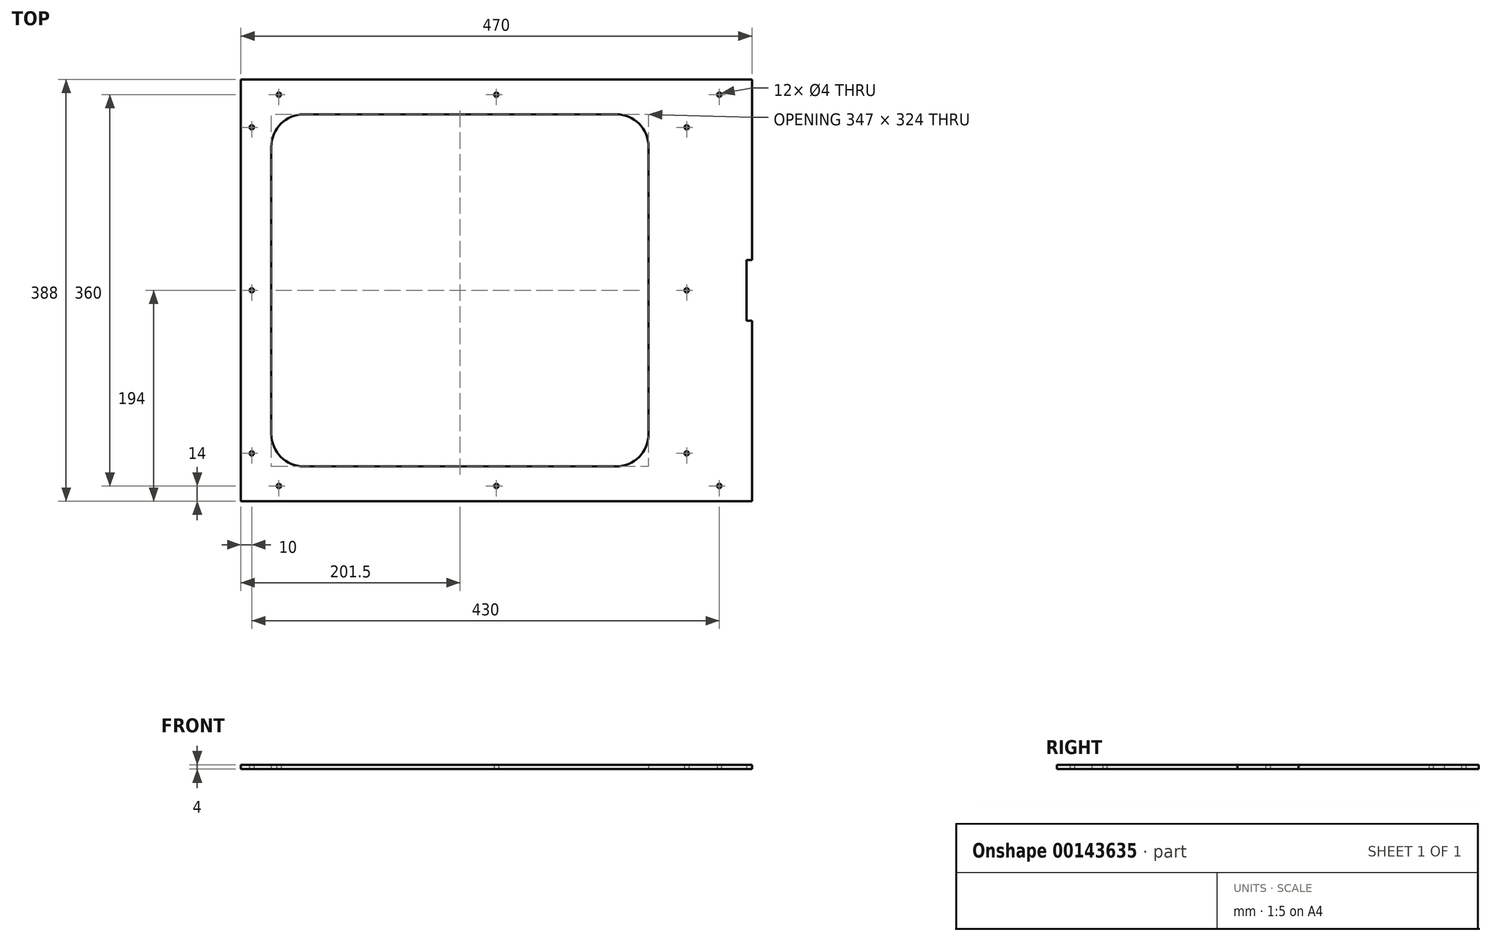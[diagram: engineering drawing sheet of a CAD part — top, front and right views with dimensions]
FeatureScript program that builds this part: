
annotation { "Feature Type Name" : "Feature", "Feature Type Description" : "" }
export const myFeature = defineFeature(function(context is Context, id is Id, definition is map)
    precondition{}
    {
        {
            var Q0;
            Q0=qCreatedBy(makeId("Top.planeOp"),FACE);
            var sketch = newSketch(context, id + "F0", { "sketchPlane" : qUnion([Q0])});
            skLineSegment(sketch, "E0.bottom", {"start": v(-235, 190) * mm, "end": v(235, 190) * mm, "construction": true});
            skLineSegment(sketch, "E0.top", {"start": v(-235, -190) * mm, "end": v(235, -190) * mm, "construction": true});
            skLineSegment(sketch, "E0.left", {"start": v(-235, 190) * mm, "end": v(-235, -190) * mm});
            skLineSegment(sketch, "E0.right", {"start": v(235, 190) * mm, "end": v(235, 28) * mm});
            skPoint(sketch, "E0.middle", {"position": v(0, 0) * mm});
            skLineSegment(sketch, "E1.bottom", {"start": v(-235, -190) * mm, "end": v(-215, -190) * mm});
            skLineSegment(sketch, "E1.top", {"start": v(-235, -170) * mm, "end": v(-215, -170) * mm, "construction": true});
            skLineSegment(sketch, "E1.left", {"start": v(-235, -190) * mm, "end": v(-235, -170) * mm});
            skLineSegment(sketch, "E1.right", {"start": v(-215, -190) * mm, "end": v(-215, -170) * mm, "construction": true});
            skLineSegment(sketch, "E2", {"start": v(-235, 0) * mm, "end": v(-215, 0) * mm, "construction": true});
            skLineSegment(sketch, "E3", {"start": v(0, -190) * mm, "end": v(0, 0) * mm, "construction": true});
            skLineSegment(sketch, "E4.MirrorCS", {"start": v(-215, 190) * mm, "end": v(-215, 170) * mm, "construction": true});
            skLineSegment(sketch, "E5.MirrorCS", {"start": v(235, -170) * mm, "end": v(215, -170) * mm, "construction": true});
            skLineSegment(sketch, "E6", {"start": v(-215, -170) * mm, "end": v(175, -170) * mm, "construction": true});
            skLineSegment(sketch, "E7", {"start": v(-215, -170) * mm, "end": v(-215, 0) * mm, "construction": true});
            skLineSegment(sketch, "E8.top", {"start": v(235, 194) * mm, "end": v(-235, 194) * mm});
            skLineSegment(sketch, "E8.left", {"start": v(235, 190) * mm, "end": v(235, 194) * mm});
            skLineSegment(sketch, "E8.right", {"start": v(-235, 190) * mm, "end": v(-235, 194) * mm});
            skLineSegment(sketch, "E9.MirrorCS", {"start": v(235, -194) * mm, "end": v(-235, -194) * mm});
            skLineSegment(sketch, "E10.MirrorCS", {"start": v(-235, -190) * mm, "end": v(-235, -194) * mm});
            skPoint(sketch, "E11", {"position": v(175, -194) * mm});
            skLineSegment(sketch, "E12", {"start": v(175, -194) * mm, "end": v(175, -190) * mm, "construction": true});
            skLineSegment(sketch, "E13.bottom", {"start": v(-177, -162) * mm, "end": v(110, -162) * mm});
            skLineSegment(sketch, "E13.left", {"start": v(-207, -132) * mm, "end": v(-207, 0) * mm});
            skLineSegment(sketch, "E13.right", {"start": v(140, -132) * mm, "end": v(140, 0) * mm});
            skPoint(sketch, "E14.visualSharp", {"position": v(-207, -162) * mm});
            skArc(sketch, "E14.filletArc", {"start": v(-207, -132) * mm, "mid": v(-198.21, -153.21) * mm, "end": v(-177, -162) * mm});
            skPoint(sketch, "E15.visualSharp", {"position": v(140, -162) * mm});
            skArc(sketch, "E15.filletArc", {"start": v(110, -162) * mm, "mid": v(131.21, -153.21) * mm, "end": v(140, -132) * mm});
            skLineSegment(sketch, "E16.MirrorCS", {"start": v(-207, 132) * mm, "end": v(-207, 0) * mm});
            skArc(sketch, "E17.MirrorCS", {"start": v(-207, 132) * mm, "mid": v(-198.21, 153.21) * mm, "end": v(-177, 162) * mm});
            skLineSegment(sketch, "E18.MirrorCS", {"start": v(-177, 162) * mm, "end": v(110, 162) * mm});
            skLineSegment(sketch, "E19.MirrorCS", {"start": v(140, 132) * mm, "end": v(140, 0) * mm});
            skArc(sketch, "E20.MirrorCS", {"start": v(110, 162) * mm, "mid": v(131.21, 153.21) * mm, "end": v(140, 132) * mm});
            skLineSegment(sketch, "E21", {"start": v(235, -190) * mm, "end": v(235, -194) * mm});
            skCircle(sketch, "E22", {"center": v(175, 0) * mm, "radius": 2 * mm});
            skLineSegment(sketch, "E23", {"start": v(175, -170) * mm, "end": v(215, -170) * mm, "construction": true});
            skLineSegment(sketch, "E24", {"start": v(175, -190) * mm, "end": v(175, -170) * mm, "construction": true});
            skLineSegment(sketch, "E25", {"start": v(175, -170) * mm, "end": v(175, -130) * mm, "construction": true});
            skLineSegment(sketch, "E26", {"start": v(175, -130) * mm, "end": v(175, 194) * mm, "construction": true});
            skCircle(sketch, "E27", {"center": v(175, -150) * mm, "radius": 2 * mm});
            skLineSegment(sketch, "E28", {"start": v(175, -180) * mm, "end": v(-20, -180) * mm, "construction": true});
            skLineSegment(sketch, "E29", {"start": v(175, -180) * mm, "end": v(235, -180) * mm, "construction": true});
            skCircle(sketch, "E30", {"center": v(205, -180) * mm, "radius": 2 * mm});
            skLineSegment(sketch, "E31", {"start": v(-20, -180) * mm, "end": v(-215, -180) * mm, "construction": true});
            skCircle(sketch, "E32.MirrorC", {"center": v(205, 180) * mm, "radius": 2 * mm});
            skCircle(sketch, "E33.MirrorC", {"center": v(-200, 180) * mm, "radius": 2 * mm});
            skLineSegment(sketch, "E34.MirrorCS", {"start": v(0, 190) * mm, "end": v(0, 0) * mm, "construction": true});
            skLineSegment(sketch, "E35.MirrorCS", {"start": v(235, -190) * mm, "end": v(235, -28) * mm});
            skLineSegment(sketch, "E36.MirrorCS", {"start": v(175, 190) * mm, "end": v(175, 170) * mm, "construction": true});
            skLineSegment(sketch, "E37.MirrorCS", {"start": v(175, 180) * mm, "end": v(235, 180) * mm, "construction": true});
            skCircle(sketch, "E38.MirrorC", {"center": v(175, 150) * mm, "radius": 2 * mm});
            skLineSegment(sketch, "E39", {"start": v(-215, 0) * mm, "end": v(-215, 170) * mm, "construction": true});
            skLineSegment(sketch, "E40", {"start": v(-215, 0) * mm, "end": v(-137.24, 0) * mm, "construction": true});
            skCircle(sketch, "E41", {"center": v(-225, 0) * mm, "radius": 2 * mm});
            skCircle(sketch, "E42", {"center": v(-225, 150) * mm, "radius": 2 * mm});
            skLineSegment(sketch, "E43", {"start": v(175, 180) * mm, "end": v(0, 180) * mm, "construction": true});
            skLineSegment(sketch, "E44", {"start": v(0, 180) * mm, "end": v(-215, 180) * mm, "construction": true});
            skCircle(sketch, "E45", {"center": v(0, 180) * mm, "radius": 2 * mm});
            skCircle(sketch, "E46.MirrorC", {"center": v(-225, -150) * mm, "radius": 2 * mm});
            skCircle(sketch, "E47.MirrorC", {"center": v(0, -180) * mm, "radius": 2 * mm});
            skCircle(sketch, "E48.MirrorC", {"center": v(-200, -180) * mm, "radius": 2 * mm});
            skLineSegment(sketch, "E49.bottom", {"start": v(174.03, 303.47) * mm, "end": v(174.03, 401.6) * mm});
            skLineSegment(sketch, "E49.top", {"start": v(214.76, 303.47) * mm, "end": v(214.76, 401.6) * mm});
            skCircle(sketch, "E50.MirrorC", {"center": v(191.67, 426.9) * mm, "radius": 10 * mm});
            skCircle(sketch, "E51", {"center": v(213.18, 437.38) * mm, "radius": 1.5 * mm});
            skLineSegment(sketch, "E49.left", {"start": v(174.03, 303.47) * mm, "end": v(214.76, 303.47) * mm});
            skCircle(sketch, "E52", {"center": v(213.18, 292.2) * mm, "radius": 1.5 * mm});
            skLineSegment(sketch, "E49.right", {"start": v(174.03, 401.6) * mm, "end": v(214.76, 401.6) * mm});
            skCircle(sketch, "E53", {"center": v(163.23, 292.38) * mm, "radius": 1.5 * mm});
            skCircle(sketch, "E54", {"center": v(163.18, 437.38) * mm, "radius": 1.5 * mm});
            skLineSegment(sketch, "E55.top", {"start": v(235, 28) * mm, "end": v(230, 28) * mm});
            skLineSegment(sketch, "E55.right", {"start": v(230, 0) * mm, "end": v(230, 28) * mm});
            skLineSegment(sketch, "E56.MirrorCS", {"start": v(230, 0) * mm, "end": v(230, -28) * mm});
            skLineSegment(sketch, "E57.MirrorCS", {"start": v(235, -28) * mm, "end": v(230, -28) * mm});
            skLineSegment(sketch, "E58.trimOffspring", {"start": v(235, -28) * mm, "end": v(235, -190) * mm});
            skLineSegment(sketch, "E59.trimOffspring", {"start": v(235, 28) * mm, "end": v(235, 190) * mm});
            skSolve(sketch);
        }
        {
            var Q0;
            Q0=makeQuery(id+"F0.imprint","IMPRINT",FACE,{"disambiguationData":[TD([[makeQuery(id+"F0.imprint","IMPRINT",EDGE,{"derivedFrom":sQuery(id+"F0.wireOp",EDGE,"209ff420-4bb6-4f9b-a423-d3239ede89f50.MirrorC")}),-1.0]])]});
            var Q1;
            {var subQ2=sQuery(id+"F0.wireOp",EDGE,"E1.right");Q1=makeQuery(id+"F0.imprint","IMPRINT",FACE,{"disambiguationData":[TD([[makeQuery(id+"F0.imprint","IMPRINT",EDGE,{"derivedFrom":subQ2}),-1.0]])]});}
            var Q2;
            Q2=makeQuery(id+"F0.imprint","IMPRINT",FACE,{"disambiguationData":[TD([[makeQuery(id+"F0.imprint","IMPRINT",EDGE,{"derivedFrom":sQuery(id+"F0.wireOp",EDGE,"wbOcR5t3-yBRG-kf52-RCKl-xsM90Xmz3qXt")}),1.0]])]});
            var Q3;
            {var subQ0=sQuery(id+"F0.wireOp",EDGE,"E1.top");Q3=makeQuery(id+"F0.imprint","IMPRINT",FACE,{"disambiguationData":[TD([[makeQuery(id+"F0.imprint","IMPRINT",EDGE,{"derivedFrom":subQ0}),1.0]])]});}
            var Q4;
            Q4=makeQuery(id+"F0.imprint","IMPRINT",FACE,{"disambiguationData":[TD([[makeQuery(id+"F0.imprint","IMPRINT",EDGE,{"derivedFrom":sQuery(id+"F0.wireOp",EDGE,"E1.bottom")}),1.0]])]});
            var Q5;
            {var subQ3=sQuery(id+"F0.wireOp",EDGE,"E4.MirrorCS");Q5=makeQuery(id+"F0.imprint","IMPRINT",FACE,{"disambiguationData":[TD([[makeQuery(id+"F0.imprint","IMPRINT",EDGE,{"derivedFrom":subQ3}),-1.0]])]});}
            var Q6;
            {var subQ0=sQuery(id+"F0.wireOp",EDGE,"E1.bottom");Q6=makeQuery(id+"F0.imprint","IMPRINT",FACE,{"disambiguationData":[TD([[makeQuery(id+"F0.imprint","IMPRINT",EDGE,{"derivedFrom":subQ0}),-1.0]])]});}
            var Q7;
            {var subQ0=sQuery(id+"F0.wireOp",EDGE,"E8.right");Q7=makeQuery(id+"F0.imprint","IMPRINT",FACE,{"disambiguationData":[TD([[makeQuery(id+"F0.imprint","IMPRINT",EDGE,{"derivedFrom":subQ0}),-1.0]])]});}
            extrude(context, id + "F1", {"entities" : qUnion([Q0, Q1, Q2, Q3, Q4, Q5, Q6, Q7]), "depth" : 4 * mm});
        }
    });
